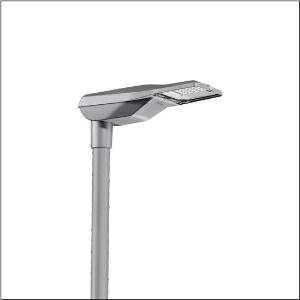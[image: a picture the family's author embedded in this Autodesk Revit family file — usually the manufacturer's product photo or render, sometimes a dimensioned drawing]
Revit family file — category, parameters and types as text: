
# Revit family: streetlight_sl_21_iq_micro___st0_8a_5xe1c31g08db_5951
name_source: partatom
category: Lighting Fixtures
units: mm (PartAtom-declared; Revit-internal decimal feet)

## family parameters
Cut with Voids When Loaded = No
Host = Face
Light Source = No
Part Type = Normal
Room Calculation Point = No
Round Connector Dimension = Use Diameter
Shared = No

## types (1)
- --- (1 x LED, 4810 lm, 36.4 W, 3000K)
    Apparent Load = 36 VA
    CIE Flux Codes = 38 75 97 100 100
    Color Rendering = 70
    Color Temperature = 3000K
    Default Elevation = 1800 mm
    Description = Streetlight SL 21 iQ micro, mast luminaire, primary light control with lens, of PMMA, primary optical cover: cover, of toughened safety glass, transparent, light distribution: ST0.8a, light emission: direct distribution, primary light characteristic: asymmetric, installation type: post-top, side-entry, LED, High Power LED, rated luminous flux: 4.810lm, luminous efficacy: 132lm/W, light colour: 730, colour temperature: 3000K, control: Street-Remote, Auto-Match, Temp-Guard, Lumen-Switch, Night-Set, Smart-Wire, Light-Fading, Desk-Remote (wireless, voltage-free reading and setting of iQ features in the workshop via application-optimized NFC function/RFID function), optimised constant luminous flux control (CLO 2.0), pre-setting: linear dimming characteristic, mains connection: 220..240V, AC, 50/60Hz, start of lifetime: 36W, end of service life: 38W, reduction: 16W, luminaire housing, of diecast aluminium, powder-coated, Siteco® metallic grey (DB 702S), corrosivity category C5 mid according to DIN EN ISO 12944, please order mast flange separately, inclination adjustable: 0°, 5°, 10°, 15°, sealing non-destructively replaceable, multi-level sealing system, length: 528mm, width: 235mm, height: 110mm, mast flange for spigot size: 42mm (side-entry): 5XC10008XM4, 60/48mm (side-entry/post-top): 5XC10108XM2, 76/60mm (side-entry/post-top): 5XC10108XM1, protection rating (complete): IP66, insulation class (complete): insulation class II (safety insulation), certification: CE, ENEC, ENEC+, VDE, impact resistance: IK09, permissible operating ambient temperature for outdoor applications: -40..+50°C, standard-compliant lighting for roads and squares, packaging unit: 1 piece

Light Distribution: ST0.8a
    Height = 110 mm
    Lamp = 1 x LED
    Lamp Light Flux = 4810 lm
    Lamp Power = 36.4 W
    Lamp count = 1
    Length = 528 mm
    Luminous efficacy = 132 lm/W
    Manufacturer = Siteco
    ModVariant = No
    Model = 5XE1C31G08DB
    Number of Poles = 1
    OnlyDefault = Yes
    Power Factor = 1
    Product Name = Streetlight SL 21 iQ micro | ST0.8a
    Product group = mast luminaire | pylon top
    ProductGroupID = 6100
    Protection Class = Protection class II
    Protection Degree = IP 66
    RLX_Detail_Level = 1
    RLX_Emergency_Light_Flux = 0 lm
    RLX_Emergency_Type = 0
    RLX_Emergency_Type_DB = No
    RlxData = <blob elided: 99149 chars, md5=93ea6f37>
    Socket = socket
    Standby Power = 0 W
    System Light Flux = 4810 lm
    System Power = 36 W
    Type Comments = factory setting: luminous flux: 100 % | dim-lin: 254 | 715 mA
    Type Image = l_1006881.jpg
    URL = http://relux.com
    VarID = @adj_124913
    Voltage = 0 V
    Weight = 0.00 kg
    Width = 235 mm

## geometry (parser evidence)
native form markers: Blend x4, Sweep x10
no freeform markers — native parametric forms only
